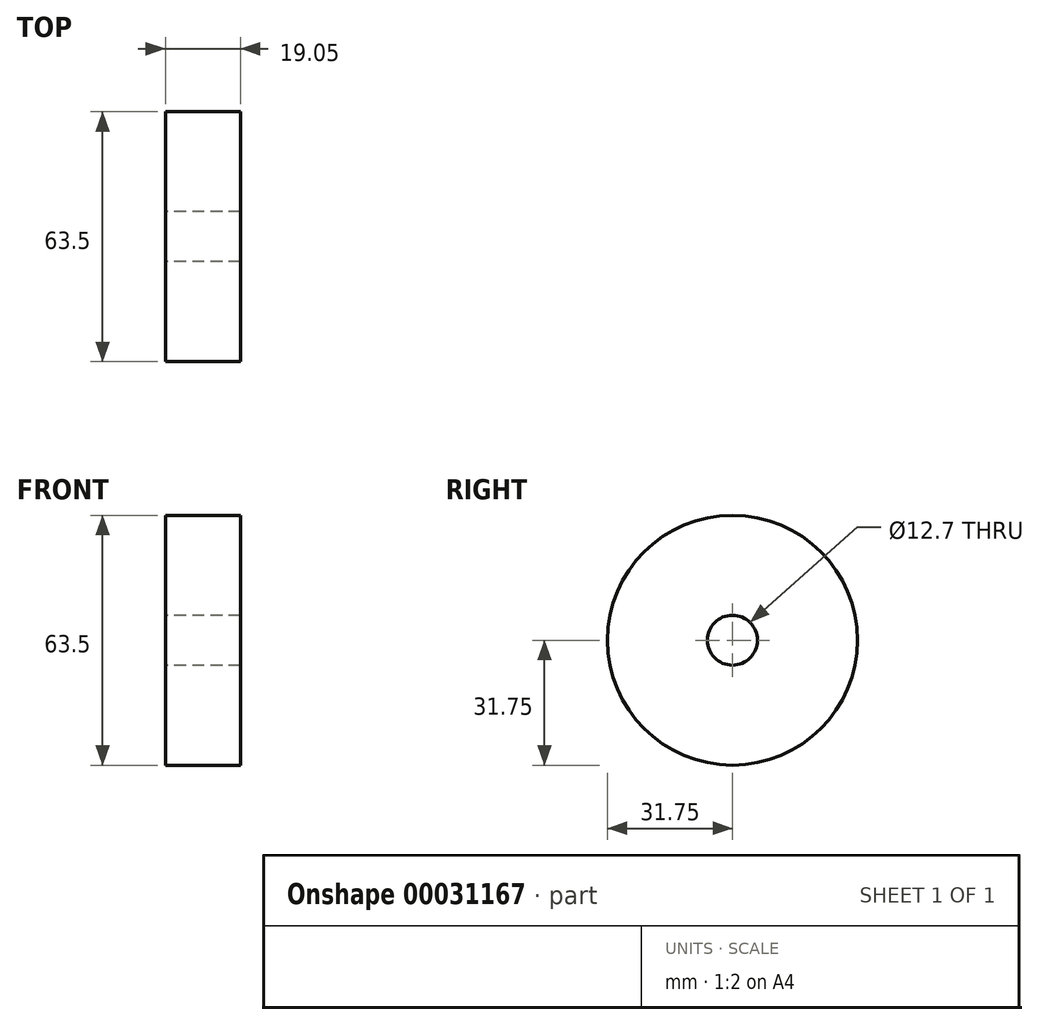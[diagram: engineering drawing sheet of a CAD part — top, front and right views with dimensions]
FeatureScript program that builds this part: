
annotation { "Feature Type Name" : "Feature", "Feature Type Description" : "" }
export const myFeature = defineFeature(function(context is Context, id is Id, definition is map)
    precondition{}
    {
        {
            var Q0;
            Q0=qCreatedBy(makeId("Right.planeOp"),FACE);
            var sketch = newSketch(context, id + "F0", { "sketchPlane" : qUnion([Q0])});
            skCircle(sketch, "E0", {"center": v(0, 0) * mm, "radius": 31.75 * mm});
            skCircle(sketch, "E1", {"center": v(0, 0) * mm, "radius": 6.35 * mm});
            skSolve(sketch);
        }
        {
            var Q0;
            Q0 = qSketchRegion(id + "F0", true);
            extrude(context, id + "F1", {"entities" : qUnion([Q0]), "depth" : 19.05 * mm});
        }
    });
